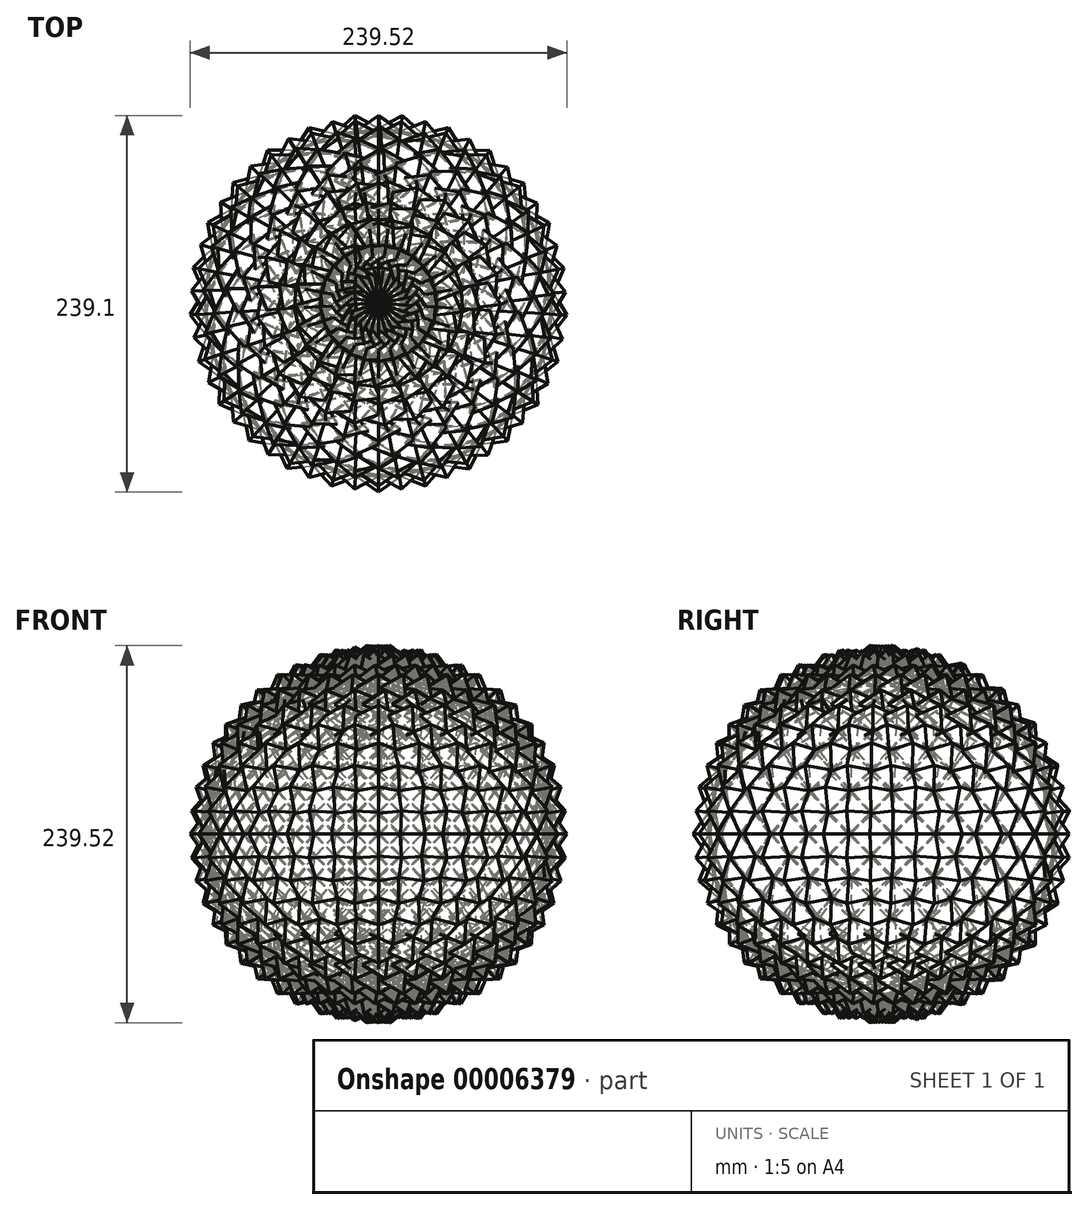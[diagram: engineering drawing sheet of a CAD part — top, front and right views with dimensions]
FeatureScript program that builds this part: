
annotation { "Feature Type Name" : "Feature", "Feature Type Description" : "" }
export const myFeature = defineFeature(function(context is Context, id is Id, definition is map)
    precondition{}
    {
        {
            var Q0;
            Q0=qCreatedBy(makeId("Front.planeOp"),FACE);
            var sketch = newSketch(context, id + "F0", { "sketchPlane" : qUnion([Q0])});
            skLineSegment(sketch, "E0.bottom", {"start": v(14, 0) * mm, "end": v(-0.14, 14.14) * mm});
            skLineSegment(sketch, "E0.top", {"start": v(-0.14, -14.14) * mm, "end": v(-14.28, 0) * mm});
            skLineSegment(sketch, "E0.left", {"start": v(-0.14, 14.14) * mm, "end": v(-14.28, 0) * mm});
            skLineSegment(sketch, "E0.right", {"start": v(14, 0) * mm, "end": v(-0.14, -14.14) * mm});
            skSolve(sketch);
        }
        {
            var Q0;
            Q0=makeQuery(id+"F0.imprint","IMPRINT",FACE,{"disambiguationData":[TD([[makeQuery(id+"F0.imprint","IMPRINT",EDGE,{"derivedFrom":sQuery(id+"F0.wireOp",EDGE,"E0.bottom")}),1.0]])]});
            extrude(context, id + "F1", {"entities" : qUnion([Q0]), "depth" : 120 * mm});
        }
        {
            var Q0;
            Q0=makeQuery(id+"F1.opExtrude","CAP_EDGE",EDGE,{"disambiguationData":[OSD([sQuery(id+"F0.wireOp",EDGE,"E0.left")])],"isStart":false});
            var Q1;
            Q1=makeQuery(id+"F1.opExtrude","CAP_EDGE",EDGE,{"disambiguationData":[OSD([sQuery(id+"F0.wireOp",EDGE,"E0.top")])],"isStart":false});
            var Q2;
            Q2=makeQuery(id+"F1.opExtrude","CAP_EDGE",EDGE,{"disambiguationData":[OSD([sQuery(id+"F0.wireOp",EDGE,"E0.right")])],"isStart":false});
            var Q3;
            Q3=makeQuery(id+"F1.opExtrude","CAP_EDGE",EDGE,{"disambiguationData":[OSD([sQuery(id+"F0.wireOp",EDGE,"E0.bottom")])],"isStart":false});
            chamfer(context, id + "F2", {"entities" : qUnion([Q0, Q1, Q2, Q3]), "width" : 10 * mm, "tangentPropagation" : true});
        }
        {
            var Q0;
            Q0=qCreatedBy(makeId("Right.planeOp"),FACE);
            var sketch = newSketch(context, id + "F3", { "sketchPlane" : qUnion([Q0])});
            skLineSegment(sketch, "E1", {"start": v(0, 0) * mm, "end": v(0, 110) * mm});
            skArc(sketch, "E2", {"start": v(0, 110) * mm, "mid": v(-110, 0) * mm, "end": v(0, -110) * mm});
            skLineSegment(sketch, "E3", {"start": v(0, 0) * mm, "end": v(0, -110) * mm});
            skSolve(sketch);
        }
        {
            var Q0;
            Q0=makeQuery(id+"F3.imprint","IMPRINT",FACE,{"disambiguationData":[TD([[makeQuery(id+"F3.imprint","IMPRINT",EDGE,{"derivedFrom":sQuery(id+"F3.wireOp",EDGE,"E1")}),1.0]])]});
            var Q1;
            Q1=sQuery(id+"F3.wireOp",EDGE,"E2");
            var Q2;
            Q2=sQuery(id+"F3.wireOp",EDGE,"E1");
            revolve(context, id + "F4", {"entities" : qUnion([Q0]), "surfaceEntities" : qUnion([Q1]), "axis" : qUnion([Q2]), "revolveType" : RevolveType.FULL});
        }
        {
            var Q0;
            Q0=makeQuery(id+"F4.opRevolve","SWEPT_BODY",BODY,{"disambiguationData":[OSD([sQuery(id+"F3.wireOp",EDGE,"E1"),sQuery(id+"F3.wireOp",EDGE,"E2"),sQuery(id+"F3.wireOp",EDGE,"E3")])]});
            var Q1;
            Q1=makeQuery(id+"F1.opExtrude","SWEPT_BODY",BODY,{"disambiguationData":[OSD([sQuery(id+"F0.wireOp",EDGE,"E0.bottom"),sQuery(id+"F0.wireOp",EDGE,"E0.top"),sQuery(id+"F0.wireOp",EDGE,"E0.left"),sQuery(id+"F0.wireOp",EDGE,"E0.right")])]});
            booleanBodies(context, id + "F5", {"operationType" : BooleanOperationType.SUBTRACTION, "tools" : qUnion([Q0]), "targets" : qUnion([Q1])});
        }
        {
            var Q0;
            Q0=qCreatedBy(makeId("Top.planeOp"),FACE);
            var sketch = newSketch(context, id + "F6", { "sketchPlane" : qUnion([Q0])});
            skCircle(sketch, "E4", {"center": v(0, 0) * mm, "radius": 110 * mm});
            skLineSegment(sketch, "E5", {"start": v(0, 0) * mm, "end": v(0, -110) * mm, "construction": true});
            skSolve(sketch);
        }
        {
            var Q0;
            Q0=qCreatedBy(makeId("Right.planeOp"),FACE);
            var sketch = newSketch(context, id + "F7", { "sketchPlane" : qUnion([Q0])});
            skCircle(sketch, "E6", {"center": v(0, 0) * mm, "radius": 110 * mm});
            skSolve(sketch);
        }
        {
            var Q0;
            Q0=sQuery(id+"F6.wireOp",EDGE,"E5");
            cPlane(context, id + "F8", {"entities" : qUnion([Q0]), "cplaneType" : CPlaneType.LINE_ANGLE, "offset" : 150 * mm, "angle" : 45 * degree, "width" : 150 * mm, "height" : 150 * mm});
        }
        {
            var Q0;
            Q0=qCreatedBy(id+"F8.planeOp",FACE);
            var sketch = newSketch(context, id + "F9", { "sketchPlane" : qUnion([Q0])});
            skCircle(sketch, "E7", {"center": v(0, 0) * mm, "radius": 110 * mm});
            skSolve(sketch);
        }
        {
            var Q0;
            Q0=makeQuery(id+"F1.opExtrude","SWEPT_BODY",BODY,{"disambiguationData":[OSD([sQuery(id+"F0.wireOp",EDGE,"E0.bottom"),sQuery(id+"F0.wireOp",EDGE,"E0.top"),sQuery(id+"F0.wireOp",EDGE,"E0.left"),sQuery(id+"F0.wireOp",EDGE,"E0.right")])]});
            var Q1;
            Q1=sQuery(id+"F9.wireOp",EDGE,"E7");
            circularPattern(context, id + "F10", {"entities" : qUnion([Q0]), "axis" : qUnion([Q1]), "angle" : 10.3 * degree, "instanceCount" : 2, "equalSpace" : true});
        }
        {
            var Q0;
            Q0=makeQuery(id+"F1.opExtrude","SWEPT_BODY",BODY,{"disambiguationData":[OSD([sQuery(id+"F0.wireOp",EDGE,"E0.bottom"),sQuery(id+"F0.wireOp",EDGE,"E0.top"),sQuery(id+"F0.wireOp",EDGE,"E0.left"),sQuery(id+"F0.wireOp",EDGE,"E0.right")])]});
            var Q1;
            Q1=sQuery(id+"F7.wireOp",EDGE,"E6");
            circularPattern(context, id + "F11", {"entities" : qUnion([Q0]), "axis" : qUnion([Q1]), "angle" : 360 * degree, "instanceCount" : 25, "equalSpace" : true});
        }
        {
            var Q0;
            Q0=makeQuery(id+"F1.opExtrude","SWEPT_BODY",BODY,{"disambiguationData":[OSD([sQuery(id+"F0.wireOp",EDGE,"E0.bottom"),sQuery(id+"F0.wireOp",EDGE,"E0.top"),sQuery(id+"F0.wireOp",EDGE,"E0.left"),sQuery(id+"F0.wireOp",EDGE,"E0.right")])]});
            var Q1;
            Q1=sQuery(id+"F6.wireOp",EDGE,"E4");
            circularPattern(context, id + "F12", {"entities" : qUnion([Q0]), "axis" : qUnion([Q1]), "angle" : 360 * degree, "instanceCount" : 25, "equalSpace" : true});
        }
        {
            var Q0;
            Q0=makeQuery(id+"F10.opPattern","COPY",BODY,{"derivedFrom":makeQuery(id+"F1.opExtrude","SWEPT_BODY",BODY,{"disambiguationData":[OSD([sQuery(id+"F0.wireOp",EDGE,"E0.bottom"),sQuery(id+"F0.wireOp",EDGE,"E0.top"),sQuery(id+"F0.wireOp",EDGE,"E0.left"),sQuery(id+"F0.wireOp",EDGE,"E0.right")])]}),"instanceName":"1"});
            var Q1;
            Q1=sQuery(id+"F7.wireOp",EDGE,"E6");
            circularPattern(context, id + "F13", {"entities" : qUnion([Q0]), "axis" : qUnion([Q1]), "angle" : 360 * degree, "instanceCount" : 25, "equalSpace" : true});
        }
        {
            var Q0;
            Q0=makeQuery(id+"F10.opPattern","COPY",BODY,{"derivedFrom":makeQuery(id+"F1.opExtrude","SWEPT_BODY",BODY,{"disambiguationData":[OSD([sQuery(id+"F0.wireOp",EDGE,"E0.bottom"),sQuery(id+"F0.wireOp",EDGE,"E0.top"),sQuery(id+"F0.wireOp",EDGE,"E0.left"),sQuery(id+"F0.wireOp",EDGE,"E0.right")])]}),"instanceName":"1"});
            var Q1;
            Q1=makeQuery(id+"F13.opPattern","COPY",BODY,{"derivedFrom":makeQuery(id+"F10.opPattern","COPY",BODY,{"derivedFrom":makeQuery(id+"F1.opExtrude","SWEPT_BODY",BODY,{"disambiguationData":[OSD([sQuery(id+"F0.wireOp",EDGE,"E0.bottom"),sQuery(id+"F0.wireOp",EDGE,"E0.top"),sQuery(id+"F0.wireOp",EDGE,"E0.left"),sQuery(id+"F0.wireOp",EDGE,"E0.right")])]}),"instanceName":"1"}),"instanceName":"24"});
            var Q2;
            Q2=sQuery(id+"F6.wireOp",EDGE,"E4");
            circularPattern(context, id + "F14", {"entities" : qUnion([Q0, Q1]), "axis" : qUnion([Q2]), "angle" : 360 * degree, "instanceCount" : 25, "equalSpace" : true});
        }
        {
            var Q0;
            Q0=makeQuery(id+"F11.opPattern","COPY",BODY,{"derivedFrom":makeQuery(id+"F1.opExtrude","SWEPT_BODY",BODY,{"disambiguationData":[OSD([sQuery(id+"F0.wireOp",EDGE,"E0.bottom"),sQuery(id+"F0.wireOp",EDGE,"E0.top"),sQuery(id+"F0.wireOp",EDGE,"E0.left"),sQuery(id+"F0.wireOp",EDGE,"E0.right")])]}),"instanceName":"24"});
            var Q1;
            Q1=makeQuery(id+"F11.opPattern","COPY",BODY,{"derivedFrom":makeQuery(id+"F1.opExtrude","SWEPT_BODY",BODY,{"disambiguationData":[OSD([sQuery(id+"F0.wireOp",EDGE,"E0.bottom"),sQuery(id+"F0.wireOp",EDGE,"E0.top"),sQuery(id+"F0.wireOp",EDGE,"E0.left"),sQuery(id+"F0.wireOp",EDGE,"E0.right")])]}),"instanceName":"1"});
            var Q2;
            Q2=sQuery(id+"F6.wireOp",EDGE,"E4");
            circularPattern(context, id + "F15", {"entities" : qUnion([Q0, Q1]), "axis" : qUnion([Q2]), "angle" : 360 * degree, "instanceCount" : 25, "equalSpace" : true});
        }
        {
            var Q0;
            Q0=makeQuery(id+"F13.opPattern","COPY",BODY,{"derivedFrom":makeQuery(id+"F10.opPattern","COPY",BODY,{"derivedFrom":makeQuery(id+"F1.opExtrude","SWEPT_BODY",BODY,{"disambiguationData":[OSD([sQuery(id+"F0.wireOp",EDGE,"E0.bottom"),sQuery(id+"F0.wireOp",EDGE,"E0.top"),sQuery(id+"F0.wireOp",EDGE,"E0.left"),sQuery(id+"F0.wireOp",EDGE,"E0.right")])]}),"instanceName":"1"}),"instanceName":"23"});
            var Q1;
            Q1=makeQuery(id+"F13.opPattern","COPY",BODY,{"derivedFrom":makeQuery(id+"F10.opPattern","COPY",BODY,{"derivedFrom":makeQuery(id+"F1.opExtrude","SWEPT_BODY",BODY,{"disambiguationData":[OSD([sQuery(id+"F0.wireOp",EDGE,"E0.bottom"),sQuery(id+"F0.wireOp",EDGE,"E0.top"),sQuery(id+"F0.wireOp",EDGE,"E0.left"),sQuery(id+"F0.wireOp",EDGE,"E0.right")])]}),"instanceName":"1"}),"instanceName":"1"});
            var Q2;
            Q2=sQuery(id+"F6.wireOp",EDGE,"E4");
            circularPattern(context, id + "F16", {"entities" : qUnion([Q0, Q1]), "axis" : qUnion([Q2]), "angle" : 360 * degree, "instanceCount" : 25, "equalSpace" : true});
        }
        {
            var Q0;
            Q0=makeQuery(id+"F11.opPattern","COPY",BODY,{"derivedFrom":makeQuery(id+"F1.opExtrude","SWEPT_BODY",BODY,{"disambiguationData":[OSD([sQuery(id+"F0.wireOp",EDGE,"E0.bottom"),sQuery(id+"F0.wireOp",EDGE,"E0.top"),sQuery(id+"F0.wireOp",EDGE,"E0.left"),sQuery(id+"F0.wireOp",EDGE,"E0.right")])]}),"instanceName":"23"});
            var Q1;
            Q1=makeQuery(id+"F11.opPattern","COPY",BODY,{"derivedFrom":makeQuery(id+"F1.opExtrude","SWEPT_BODY",BODY,{"disambiguationData":[OSD([sQuery(id+"F0.wireOp",EDGE,"E0.bottom"),sQuery(id+"F0.wireOp",EDGE,"E0.top"),sQuery(id+"F0.wireOp",EDGE,"E0.left"),sQuery(id+"F0.wireOp",EDGE,"E0.right")])]}),"instanceName":"2"});
            var Q2;
            Q2=sQuery(id+"F6.wireOp",EDGE,"E4");
            circularPattern(context, id + "F17", {"entities" : qUnion([Q0, Q1]), "axis" : qUnion([Q2]), "angle" : 360 * degree, "instanceCount" : 25, "equalSpace" : true});
        }
        {
            var Q0;
            Q0=makeQuery(id+"F13.opPattern","COPY",BODY,{"derivedFrom":makeQuery(id+"F10.opPattern","COPY",BODY,{"derivedFrom":makeQuery(id+"F1.opExtrude","SWEPT_BODY",BODY,{"disambiguationData":[OSD([sQuery(id+"F0.wireOp",EDGE,"E0.bottom"),sQuery(id+"F0.wireOp",EDGE,"E0.top"),sQuery(id+"F0.wireOp",EDGE,"E0.left"),sQuery(id+"F0.wireOp",EDGE,"E0.right")])]}),"instanceName":"1"}),"instanceName":"22"});
            var Q1;
            Q1=makeQuery(id+"F13.opPattern","COPY",BODY,{"derivedFrom":makeQuery(id+"F10.opPattern","COPY",BODY,{"derivedFrom":makeQuery(id+"F1.opExtrude","SWEPT_BODY",BODY,{"disambiguationData":[OSD([sQuery(id+"F0.wireOp",EDGE,"E0.bottom"),sQuery(id+"F0.wireOp",EDGE,"E0.top"),sQuery(id+"F0.wireOp",EDGE,"E0.left"),sQuery(id+"F0.wireOp",EDGE,"E0.right")])]}),"instanceName":"1"}),"instanceName":"2"});
            var Q2;
            Q2=makeQuery(id+"F11.opPattern","COPY",BODY,{"derivedFrom":makeQuery(id+"F1.opExtrude","SWEPT_BODY",BODY,{"disambiguationData":[OSD([sQuery(id+"F0.wireOp",EDGE,"E0.bottom"),sQuery(id+"F0.wireOp",EDGE,"E0.top"),sQuery(id+"F0.wireOp",EDGE,"E0.left"),sQuery(id+"F0.wireOp",EDGE,"E0.right")])]}),"instanceName":"22"});
            var Q3;
            Q3=makeQuery(id+"F13.opPattern","COPY",BODY,{"derivedFrom":makeQuery(id+"F10.opPattern","COPY",BODY,{"derivedFrom":makeQuery(id+"F1.opExtrude","SWEPT_BODY",BODY,{"disambiguationData":[OSD([sQuery(id+"F0.wireOp",EDGE,"E0.bottom"),sQuery(id+"F0.wireOp",EDGE,"E0.top"),sQuery(id+"F0.wireOp",EDGE,"E0.left"),sQuery(id+"F0.wireOp",EDGE,"E0.right")])]}),"instanceName":"1"}),"instanceName":"21"});
            var Q4;
            Q4=makeQuery(id+"F11.opPattern","COPY",BODY,{"derivedFrom":makeQuery(id+"F1.opExtrude","SWEPT_BODY",BODY,{"disambiguationData":[OSD([sQuery(id+"F0.wireOp",EDGE,"E0.bottom"),sQuery(id+"F0.wireOp",EDGE,"E0.top"),sQuery(id+"F0.wireOp",EDGE,"E0.left"),sQuery(id+"F0.wireOp",EDGE,"E0.right")])]}),"instanceName":"21"});
            var Q5;
            Q5=makeQuery(id+"F13.opPattern","COPY",BODY,{"derivedFrom":makeQuery(id+"F10.opPattern","COPY",BODY,{"derivedFrom":makeQuery(id+"F1.opExtrude","SWEPT_BODY",BODY,{"disambiguationData":[OSD([sQuery(id+"F0.wireOp",EDGE,"E0.bottom"),sQuery(id+"F0.wireOp",EDGE,"E0.top"),sQuery(id+"F0.wireOp",EDGE,"E0.left"),sQuery(id+"F0.wireOp",EDGE,"E0.right")])]}),"instanceName":"1"}),"instanceName":"20"});
            var Q6;
            Q6=makeQuery(id+"F11.opPattern","COPY",BODY,{"derivedFrom":makeQuery(id+"F1.opExtrude","SWEPT_BODY",BODY,{"disambiguationData":[OSD([sQuery(id+"F0.wireOp",EDGE,"E0.bottom"),sQuery(id+"F0.wireOp",EDGE,"E0.top"),sQuery(id+"F0.wireOp",EDGE,"E0.left"),sQuery(id+"F0.wireOp",EDGE,"E0.right")])]}),"instanceName":"20"});
            var Q7;
            Q7=makeQuery(id+"F13.opPattern","COPY",BODY,{"derivedFrom":makeQuery(id+"F10.opPattern","COPY",BODY,{"derivedFrom":makeQuery(id+"F1.opExtrude","SWEPT_BODY",BODY,{"disambiguationData":[OSD([sQuery(id+"F0.wireOp",EDGE,"E0.bottom"),sQuery(id+"F0.wireOp",EDGE,"E0.top"),sQuery(id+"F0.wireOp",EDGE,"E0.left"),sQuery(id+"F0.wireOp",EDGE,"E0.right")])]}),"instanceName":"1"}),"instanceName":"19"});
            var Q8;
            Q8=makeQuery(id+"F11.opPattern","COPY",BODY,{"derivedFrom":makeQuery(id+"F1.opExtrude","SWEPT_BODY",BODY,{"disambiguationData":[OSD([sQuery(id+"F0.wireOp",EDGE,"E0.bottom"),sQuery(id+"F0.wireOp",EDGE,"E0.top"),sQuery(id+"F0.wireOp",EDGE,"E0.left"),sQuery(id+"F0.wireOp",EDGE,"E0.right")])]}),"instanceName":"19"});
            var Q9;
            Q9=makeQuery(id+"F11.opPattern","COPY",BODY,{"derivedFrom":makeQuery(id+"F1.opExtrude","SWEPT_BODY",BODY,{"disambiguationData":[OSD([sQuery(id+"F0.wireOp",EDGE,"E0.bottom"),sQuery(id+"F0.wireOp",EDGE,"E0.top"),sQuery(id+"F0.wireOp",EDGE,"E0.left"),sQuery(id+"F0.wireOp",EDGE,"E0.right")])]}),"instanceName":"3"});
            var Q10;
            Q10=makeQuery(id+"F13.opPattern","COPY",BODY,{"derivedFrom":makeQuery(id+"F10.opPattern","COPY",BODY,{"derivedFrom":makeQuery(id+"F1.opExtrude","SWEPT_BODY",BODY,{"disambiguationData":[OSD([sQuery(id+"F0.wireOp",EDGE,"E0.bottom"),sQuery(id+"F0.wireOp",EDGE,"E0.top"),sQuery(id+"F0.wireOp",EDGE,"E0.left"),sQuery(id+"F0.wireOp",EDGE,"E0.right")])]}),"instanceName":"1"}),"instanceName":"3"});
            var Q11;
            Q11=makeQuery(id+"F11.opPattern","COPY",BODY,{"derivedFrom":makeQuery(id+"F1.opExtrude","SWEPT_BODY",BODY,{"disambiguationData":[OSD([sQuery(id+"F0.wireOp",EDGE,"E0.bottom"),sQuery(id+"F0.wireOp",EDGE,"E0.top"),sQuery(id+"F0.wireOp",EDGE,"E0.left"),sQuery(id+"F0.wireOp",EDGE,"E0.right")])]}),"instanceName":"4"});
            var Q12;
            Q12=makeQuery(id+"F13.opPattern","COPY",BODY,{"derivedFrom":makeQuery(id+"F10.opPattern","COPY",BODY,{"derivedFrom":makeQuery(id+"F1.opExtrude","SWEPT_BODY",BODY,{"disambiguationData":[OSD([sQuery(id+"F0.wireOp",EDGE,"E0.bottom"),sQuery(id+"F0.wireOp",EDGE,"E0.top"),sQuery(id+"F0.wireOp",EDGE,"E0.left"),sQuery(id+"F0.wireOp",EDGE,"E0.right")])]}),"instanceName":"1"}),"instanceName":"4"});
            var Q13;
            Q13=makeQuery(id+"F11.opPattern","COPY",BODY,{"derivedFrom":makeQuery(id+"F1.opExtrude","SWEPT_BODY",BODY,{"disambiguationData":[OSD([sQuery(id+"F0.wireOp",EDGE,"E0.bottom"),sQuery(id+"F0.wireOp",EDGE,"E0.top"),sQuery(id+"F0.wireOp",EDGE,"E0.left"),sQuery(id+"F0.wireOp",EDGE,"E0.right")])]}),"instanceName":"5"});
            var Q14;
            Q14=makeQuery(id+"F13.opPattern","COPY",BODY,{"derivedFrom":makeQuery(id+"F10.opPattern","COPY",BODY,{"derivedFrom":makeQuery(id+"F1.opExtrude","SWEPT_BODY",BODY,{"disambiguationData":[OSD([sQuery(id+"F0.wireOp",EDGE,"E0.bottom"),sQuery(id+"F0.wireOp",EDGE,"E0.top"),sQuery(id+"F0.wireOp",EDGE,"E0.left"),sQuery(id+"F0.wireOp",EDGE,"E0.right")])]}),"instanceName":"1"}),"instanceName":"5"});
            var Q15;
            Q15=makeQuery(id+"F11.opPattern","COPY",BODY,{"derivedFrom":makeQuery(id+"F1.opExtrude","SWEPT_BODY",BODY,{"disambiguationData":[OSD([sQuery(id+"F0.wireOp",EDGE,"E0.bottom"),sQuery(id+"F0.wireOp",EDGE,"E0.top"),sQuery(id+"F0.wireOp",EDGE,"E0.left"),sQuery(id+"F0.wireOp",EDGE,"E0.right")])]}),"instanceName":"6"});
            var Q16;
            Q16=sQuery(id+"F6.wireOp",EDGE,"E4");
            circularPattern(context, id + "F18", {"entities" : qUnion([Q0, Q1, Q2, Q3, Q4, Q5, Q6, Q7, Q8, Q9, Q10, Q11, Q12, Q13, Q14, Q15]), "axis" : qUnion([Q16]), "angle" : 360 * degree, "instanceCount" : 25, "equalSpace" : true});
        }
    });
